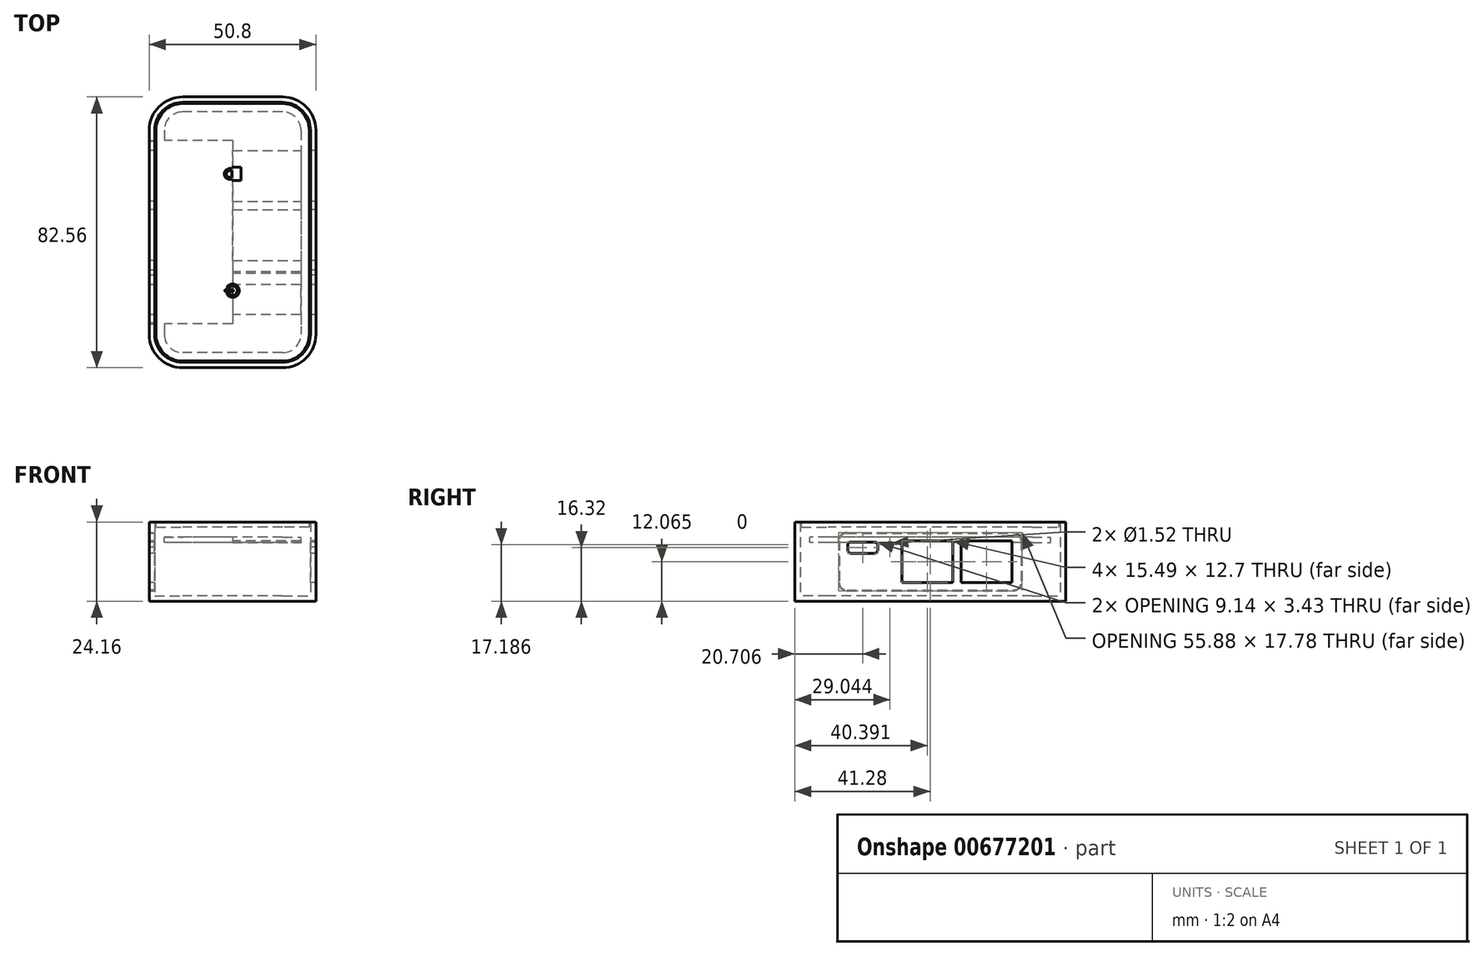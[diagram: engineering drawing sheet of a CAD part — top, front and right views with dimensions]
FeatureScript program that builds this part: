
annotation { "Feature Type Name" : "Feature", "Feature Type Description" : "" }
export const myFeature = defineFeature(function(context is Context, id is Id, definition is map)
    precondition{}
    {
        {
            var Q0;
            Q0=qCreatedBy(makeId("Top.planeOp"),FACE);
            var sketch = newSketch(context, id + "F0", { "sketchPlane" : qUnion([Q0])});
            skLineSegment(sketch, "E0.bottom", {"start": v(25.4, 41.28) * mm, "end": v(-25.4, 41.28) * mm});
            skLineSegment(sketch, "E0.top", {"start": v(25.4, -41.28) * mm, "end": v(-25.4, -41.28) * mm});
            skLineSegment(sketch, "E0.left", {"start": v(25.4, 41.28) * mm, "end": v(25.4, -41.28) * mm});
            skLineSegment(sketch, "E0.right", {"start": v(-25.4, 41.28) * mm, "end": v(-25.4, -41.28) * mm});
            skPoint(sketch, "E0.middle", {"position": v(0, 0) * mm});
            skSolve(sketch);
        }
        {
            var Q0;
            Q0=qSketchRegion(id+"F0",true);
            extrude(context, id + "F1", {"entities" : qUnion([Q0]), "depth" : 24.13 * mm, "offsetDistance" : 25.4 * mm});
        }
        {
            var Q0;
            Q0=makeQuery(id+"F1.opExtrude","SWEPT_EDGE",EDGE,{"disambiguationData":[OSD([sQuery(id+"F0.wireOp",EDGE,"E0.top"),sQuery(id+"F0.wireOp",EDGE,"E0.left")])]});
            var Q1;
            Q1=makeQuery(id+"F1.opExtrude","SWEPT_EDGE",EDGE,{"disambiguationData":[OSD([sQuery(id+"F0.wireOp",EDGE,"E0.top"),sQuery(id+"F0.wireOp",EDGE,"E0.right")])]});
            var Q2;
            Q2=makeQuery(id+"F1.opExtrude","SWEPT_EDGE",EDGE,{"disambiguationData":[OSD([sQuery(id+"F0.wireOp",EDGE,"E0.bottom"),sQuery(id+"F0.wireOp",EDGE,"E0.left")])]});
            var Q3;
            Q3=makeQuery(id+"F1.opExtrude","SWEPT_EDGE",EDGE,{"disambiguationData":[OSD([sQuery(id+"F0.wireOp",EDGE,"E0.bottom"),sQuery(id+"F0.wireOp",EDGE,"E0.right")])]});
            fillet(context, id + "F2", {"entities" : qUnion([Q0, Q1, Q2, Q3]), "radius" : 10.16 * mm, "tangentPropagation" : true, "allowEdgeOverflow" : false});
        }
        {
            var Q0;
            Q0=makeQuery(id+"F1.opExtrude","CAP_FACE",FACE,{"disambiguationData":[OSD([sQuery(id+"F0.wireOp",EDGE,"E0.bottom"),sQuery(id+"F0.wireOp",EDGE,"E0.top"),sQuery(id+"F0.wireOp",EDGE,"E0.left"),sQuery(id+"F0.wireOp",EDGE,"E0.right")])],"isStart":false});
            shell(context, id + "F3", {"entities" : qUnion([Q0]), "thickness" : 1.65 * mm});
        }
        {
            var Q0;
            Q0=makeQuery(id+"F1.opExtrude","CAP_FACE",FACE,{"disambiguationData":[OSD([sQuery(id+"F0.wireOp",EDGE,"E0.bottom"),sQuery(id+"F0.wireOp",EDGE,"E0.top"),sQuery(id+"F0.wireOp",EDGE,"E0.left"),sQuery(id+"F0.wireOp",EDGE,"E0.right")])],"isStart":false});
            var sketch = newSketch(context, id + "F4", { "sketchPlane" : qUnion([Q0])});
            skArc(sketch, "E1.0", {"start": v(-15.24, 39.24) * mm, "mid": v(-20.99, 36.86) * mm, "end": v(-23.37, 31.12) * mm});
            skLineSegment(sketch, "E1.1", {"start": v(15.24, 39.24) * mm, "end": v(-15.24, 39.24) * mm});
            skLineSegment(sketch, "E1.2", {"start": v(-23.37, 31.12) * mm, "end": v(-23.37, -31.12) * mm});
            skArc(sketch, "E1.3", {"start": v(23.37, 31.12) * mm, "mid": v(20.99, 36.86) * mm, "end": v(15.24, 39.24) * mm});
            skArc(sketch, "E1.4", {"start": v(-23.37, -31.12) * mm, "mid": v(-20.99, -36.86) * mm, "end": v(-15.24, -39.24) * mm});
            skLineSegment(sketch, "E1.5", {"start": v(15.24, -39.24) * mm, "end": v(-15.24, -39.24) * mm});
            skArc(sketch, "E1.6", {"start": v(15.24, -39.24) * mm, "mid": v(20.99, -36.86) * mm, "end": v(23.37, -31.12) * mm});
            skLineSegment(sketch, "E1.7", {"start": v(23.37, 31.12) * mm, "end": v(23.37, -31.12) * mm});
            skSolve(sketch);
        }
        {
            var Q0;
            Q0=qSketchRegion(id+"F4",true);
            extrude(context, id + "F5", {"entities" : qUnion([Q0]), "oppositeDirection" : true, "depth" : 6.35 * mm, "offsetDistance" : 25.4 * mm});
        }
        {
            var Q0;
            Q0=makeQuery(id+"F5.opExtrude","CAP_FACE",FACE,{"disambiguationData":[OSD([sQuery(id+"F4.wireOp",EDGE,"E1.0"),sQuery(id+"F4.wireOp",EDGE,"E1.1"),sQuery(id+"F4.wireOp",EDGE,"E1.2"),sQuery(id+"F4.wireOp",EDGE,"E1.3"),sQuery(id+"F4.wireOp",EDGE,"E1.4"),sQuery(id+"F4.wireOp",EDGE,"E1.5"),sQuery(id+"F4.wireOp",EDGE,"E1.6"),sQuery(id+"F4.wireOp",EDGE,"E1.7")])],"isStart":true});
            var sketch = newSketch(context, id + "F6", { "sketchPlane" : qUnion([Q0])});
            skLineSegment(sketch, "E2.0", {"start": v(15.24, 32.9) * mm, "end": v(-15.24, 32.9) * mm});
            skArc(sketch, "E2.1", {"start": v(17.02, 31.12) * mm, "mid": v(16.5, 32.37) * mm, "end": v(15.24, 32.9) * mm});
            skArc(sketch, "E2.2", {"start": v(-15.24, 32.9) * mm, "mid": v(-16.5, 32.37) * mm, "end": v(-17.02, 31.12) * mm});
            skLineSegment(sketch, "E2.3", {"start": v(17.02, 31.12) * mm, "end": v(17.02, -31.12) * mm});
            skLineSegment(sketch, "E2.4", {"start": v(-17.02, 31.12) * mm, "end": v(-17.02, -31.12) * mm});
            skArc(sketch, "E2.5", {"start": v(-17.02, -31.12) * mm, "mid": v(-16.5, -32.37) * mm, "end": v(-15.24, -32.9) * mm});
            skLineSegment(sketch, "E2.6", {"start": v(15.24, -32.9) * mm, "end": v(-15.24, -32.9) * mm});
            skArc(sketch, "E2.7", {"start": v(15.24, -32.9) * mm, "mid": v(16.5, -32.37) * mm, "end": v(17.02, -31.12) * mm});
            skSolve(sketch);
        }
        {
            var Q0;
            Q0=sQuery(id+"F6.wireOp",VERTEX,"E2.7.start");
            var Q1;
            Q1=qCreatedBy(makeId("Right.planeOp"),FACE);
            cPlane(context, id + "F7", {"entities" : qUnion([Q0, Q1]), "cplaneType" : CPlaneType.PLANE_POINT, "offset" : 25.4 * mm, "width" : 152.4 * mm, "height" : 152.4 * mm});
        }
        {
            var Q0;
            Q0=makeQuery(id+"F5.opExtrude","CAP_FACE",FACE,{"disambiguationData":[OSD([sQuery(id+"F4.wireOp",EDGE,"E1.0"),sQuery(id+"F4.wireOp",EDGE,"E1.1"),sQuery(id+"F4.wireOp",EDGE,"E1.2"),sQuery(id+"F4.wireOp",EDGE,"E1.3"),sQuery(id+"F4.wireOp",EDGE,"E1.4"),sQuery(id+"F4.wireOp",EDGE,"E1.5"),sQuery(id+"F4.wireOp",EDGE,"E1.6"),sQuery(id+"F4.wireOp",EDGE,"E1.7")])],"isStart":false});
            var Q1;
            Q1=makeQuery(id+"F5.opExtrude","SWEPT_FACE",FACE,{"disambiguationData":[OSD([sQuery(id+"F4.wireOp",EDGE,"E1.5")])]});
            var Q2;
            Q2=makeQuery(id+"F5.opExtrude","SWEPT_FACE",FACE,{"disambiguationData":[OSD([sQuery(id+"F4.wireOp",EDGE,"E1.6")])]});
            var Q3;
            Q3=makeQuery(id+"F5.opExtrude","SWEPT_FACE",FACE,{"disambiguationData":[OSD([sQuery(id+"F4.wireOp",EDGE,"E1.4")])]});
            var Q4;
            Q4=makeQuery(id+"F5.opExtrude","SWEPT_FACE",FACE,{"disambiguationData":[OSD([sQuery(id+"F4.wireOp",EDGE,"E1.7")])]});
            var Q5;
            Q5=makeQuery(id+"F5.opExtrude","SWEPT_FACE",FACE,{"disambiguationData":[OSD([sQuery(id+"F4.wireOp",EDGE,"E1.3")])]});
            var Q6;
            Q6=makeQuery(id+"F5.opExtrude","SWEPT_FACE",FACE,{"disambiguationData":[OSD([sQuery(id+"F4.wireOp",EDGE,"E1.1")])]});
            var Q7;
            Q7=makeQuery(id+"F5.opExtrude","SWEPT_FACE",FACE,{"disambiguationData":[OSD([sQuery(id+"F4.wireOp",EDGE,"E1.0")])]});
            var Q8;
            Q8=makeQuery(id+"F5.opExtrude","SWEPT_FACE",FACE,{"disambiguationData":[OSD([sQuery(id+"F4.wireOp",EDGE,"E1.2")])]});
            shell(context, id + "F8", {"entities" : qUnion([Q0, Q1, Q2, Q3, Q4, Q5, Q6, Q7, Q8]), "thickness" : 1.52 * mm});
        }
        {
            var Q0;
            Q0=makeQuery(id+"F4.imprint","IMPRINT",FACE,{"disambiguationData":[TD([[makeQuery(id+"F4.imprint","IMPRINT",EDGE,{"derivedFrom":sQuery(id+"F4.wireOp",EDGE,"E1.0")}),1.0]])]});
            var sketch = newSketch(context, id + "F9", { "sketchPlane" : qUnion([Q0])});
            skLineSegment(sketch, "E3.bottom", {"start": v(2.54, 22.86) * mm, "end": v(-2.54, 22.86) * mm});
            skLineSegment(sketch, "E3.top", {"start": v(2.54, 12.7) * mm, "end": v(-2.54, 12.7) * mm});
            skLineSegment(sketch, "E3.left", {"start": v(5.08, 20.32) * mm, "end": v(5.08, 15.24) * mm});
            skLineSegment(sketch, "E3.right", {"start": v(-5.08, 20.32) * mm, "end": v(-5.08, 15.24) * mm});
            skPoint(sketch, "E3.middle", {"position": v(0, 17.78) * mm});
            skPoint(sketch, "E4.visualSharp", {"position": v(-5.08, 22.86) * mm});
            skArc(sketch, "E4.filletArc", {"start": v(-2.54, 22.86) * mm, "mid": v(-4.34, 22.12) * mm, "end": v(-5.08, 20.32) * mm});
            skPoint(sketch, "E5.visualSharp", {"position": v(5.08, 22.86) * mm});
            skArc(sketch, "E5.filletArc", {"start": v(5.08, 20.32) * mm, "mid": v(4.34, 22.12) * mm, "end": v(2.54, 22.86) * mm});
            skPoint(sketch, "E6.visualSharp", {"position": v(5.08, 12.7) * mm});
            skArc(sketch, "E6.filletArc", {"start": v(2.54, 12.7) * mm, "mid": v(4.34, 13.44) * mm, "end": v(5.08, 15.24) * mm});
            skPoint(sketch, "E7.visualSharp", {"position": v(-5.08, 12.7) * mm});
            skArc(sketch, "E7.filletArc", {"start": v(-5.08, 15.24) * mm, "mid": v(-4.34, 13.44) * mm, "end": v(-2.54, 12.7) * mm});
            skArc(sketch, "E8.MirrorCS", {"start": v(-2.54, -22.86) * mm, "mid": v(-4.34, -22.12) * mm, "end": v(-5.08, -20.32) * mm});
            skLineSegment(sketch, "E9.MirrorCS", {"start": v(-5.08, -20.32) * mm, "end": v(-5.08, -15.24) * mm});
            skLineSegment(sketch, "E10.MirrorCS", {"start": v(5.08, -20.32) * mm, "end": v(5.08, -15.24) * mm});
            skArc(sketch, "E11.MirrorCS", {"start": v(2.54, -12.7) * mm, "mid": v(4.34, -13.44) * mm, "end": v(5.08, -15.24) * mm});
            skArc(sketch, "E12.MirrorCS", {"start": v(-5.08, -15.24) * mm, "mid": v(-4.34, -13.44) * mm, "end": v(-2.54, -12.7) * mm});
            skLineSegment(sketch, "E13.MirrorCS", {"start": v(2.54, -12.7) * mm, "end": v(-2.54, -12.7) * mm});
            skArc(sketch, "E14.MirrorCS", {"start": v(5.08, -20.32) * mm, "mid": v(4.34, -22.12) * mm, "end": v(2.54, -22.86) * mm});
            skLineSegment(sketch, "E15.MirrorCS", {"start": v(2.54, -22.86) * mm, "end": v(-2.54, -22.86) * mm});
            skSolve(sketch);
        }
        {
            var Q0;
            Q0=makeQuery(id+"F5.opExtrude","CAP_FACE",FACE,{"disambiguationData":[OSD([sQuery(id+"F4.wireOp",EDGE,"E1.0"),sQuery(id+"F4.wireOp",EDGE,"E1.1"),sQuery(id+"F4.wireOp",EDGE,"E1.2"),sQuery(id+"F4.wireOp",EDGE,"E1.3"),sQuery(id+"F4.wireOp",EDGE,"E1.4"),sQuery(id+"F4.wireOp",EDGE,"E1.5"),sQuery(id+"F4.wireOp",EDGE,"E1.6"),sQuery(id+"F4.wireOp",EDGE,"E1.7")])],"isStart":true});
            cPlane(context, id + "F10", {"entities" : qUnion([Q0]), "cplaneType" : CPlaneType.OFFSET, "offset" : 0 * mm, "width" : 152.4 * mm, "height" : 152.4 * mm});
        }
        {
            var Q0;
            Q0=qCreatedBy(id+"F10.planeOp",FACE);
            var sketch = newSketch(context, id + "F11", { "sketchPlane" : qUnion([Q0])});
            skArc(sketch, "E16.0", {"start": v(2.54, -12.95) * mm, "mid": v(4.16, -13.62) * mm, "end": v(4.83, -15.24) * mm});
            skLineSegment(sketch, "E16.1", {"start": v(4.83, -20.32) * mm, "end": v(4.83, -15.24) * mm});
            skLineSegment(sketch, "E16.2", {"start": v(2.54, -12.95) * mm, "end": v(-2.54, -12.95) * mm});
            skArc(sketch, "E16.3", {"start": v(4.83, -20.32) * mm, "mid": v(4.16, -21.94) * mm, "end": v(2.54, -22.6) * mm});
            skArc(sketch, "E16.4", {"start": v(-4.83, -15.24) * mm, "mid": v(-4.16, -13.62) * mm, "end": v(-2.54, -12.95) * mm});
            skLineSegment(sketch, "E16.5", {"start": v(-4.83, -20.32) * mm, "end": v(-4.83, -15.24) * mm});
            skArc(sketch, "E16.6", {"start": v(-2.54, -22.6) * mm, "mid": v(-4.16, -21.94) * mm, "end": v(-4.83, -20.32) * mm});
            skLineSegment(sketch, "E16.7", {"start": v(2.54, -22.6) * mm, "end": v(-2.54, -22.6) * mm});
            skArc(sketch, "E17.0", {"start": v(4.83, 20.32) * mm, "mid": v(4.16, 21.94) * mm, "end": v(2.54, 22.6) * mm});
            skLineSegment(sketch, "E17.1", {"start": v(4.83, 20.32) * mm, "end": v(4.83, 15.24) * mm});
            skLineSegment(sketch, "E17.2", {"start": v(2.54, 22.6) * mm, "end": v(-2.54, 22.6) * mm});
            skArc(sketch, "E17.3", {"start": v(2.54, 12.95) * mm, "mid": v(4.16, 13.62) * mm, "end": v(4.83, 15.24) * mm});
            skArc(sketch, "E17.4", {"start": v(-2.54, 22.6) * mm, "mid": v(-4.16, 21.94) * mm, "end": v(-4.83, 20.32) * mm});
            skLineSegment(sketch, "E17.5", {"start": v(-4.83, 20.32) * mm, "end": v(-4.83, 15.24) * mm});
            skArc(sketch, "E17.6", {"start": v(-4.83, 15.24) * mm, "mid": v(-4.16, 13.62) * mm, "end": v(-2.54, 12.95) * mm});
            skLineSegment(sketch, "E17.7", {"start": v(2.54, 12.95) * mm, "end": v(-2.54, 12.95) * mm});
            skSolve(sketch);
        }
        {
            var Q0;
            Q0=makeQuery(id+"F8.opShell","OFFSET_FACE",FACE,{"disambiguationData":[OSD([sQuery(id+"F4.wireOp",EDGE,"E1.0"),sQuery(id+"F4.wireOp",EDGE,"E1.1"),sQuery(id+"F4.wireOp",EDGE,"E1.2"),sQuery(id+"F4.wireOp",EDGE,"E1.3"),sQuery(id+"F4.wireOp",EDGE,"E1.4"),sQuery(id+"F4.wireOp",EDGE,"E1.5"),sQuery(id+"F4.wireOp",EDGE,"E1.6"),sQuery(id+"F4.wireOp",EDGE,"E1.7")])]});
            cPlane(context, id + "F12", {"entities" : qUnion([Q0]), "cplaneType" : CPlaneType.OFFSET, "offset" : 3.05 * mm, "width" : 152.4 * mm, "height" : 152.4 * mm});
        }
        {
            var Q0;
            Q0=qCreatedBy(id+"F12.planeOp",FACE);
            var sketch = newSketch(context, id + "F13", { "sketchPlane" : qUnion([Q0])});
            skLineSegment(sketch, "E18.0", {"start": v(-20.83, -31.12) * mm, "end": v(-20.83, 31.12) * mm});
            skArc(sketch, "E18.1", {"start": v(-15.24, -36.7) * mm, "mid": v(-19.2, -35.07) * mm, "end": v(-20.83, -31.12) * mm});
            skArc(sketch, "E18.2", {"start": v(-20.83, 31.12) * mm, "mid": v(-19.2, 35.07) * mm, "end": v(-15.24, 36.7) * mm});
            skLineSegment(sketch, "E18.3", {"start": v(15.24, -36.7) * mm, "end": v(-15.24, -36.7) * mm});
            skLineSegment(sketch, "E18.4", {"start": v(15.24, 36.7) * mm, "end": v(-15.24, 36.7) * mm});
            skArc(sketch, "E18.5", {"start": v(15.24, 36.7) * mm, "mid": v(19.2, 35.07) * mm, "end": v(20.83, 31.12) * mm});
            skLineSegment(sketch, "E18.6", {"start": v(20.83, -31.12) * mm, "end": v(20.83, 31.12) * mm});
            skArc(sketch, "E18.7", {"start": v(20.83, -31.12) * mm, "mid": v(19.2, -35.07) * mm, "end": v(15.24, -36.7) * mm});
            skSolve(sketch);
        }
        {
            var Q0;
            Q0=qSketchRegion(id+"F13",true);
            extrude(context, id + "F14", {"entities" : qUnion([Q0]), "depth" : 1.65 * mm, "offsetDistance" : 25.4 * mm});
        }
        {
            var Q0;
            Q0=makeQuery(id+"F5.opExtrude","CAP_FACE",FACE,{"disambiguationData":[OSD([sQuery(id+"F4.wireOp",EDGE,"E1.0"),sQuery(id+"F4.wireOp",EDGE,"E1.1"),sQuery(id+"F4.wireOp",EDGE,"E1.2"),sQuery(id+"F4.wireOp",EDGE,"E1.3"),sQuery(id+"F4.wireOp",EDGE,"E1.4"),sQuery(id+"F4.wireOp",EDGE,"E1.5"),sQuery(id+"F4.wireOp",EDGE,"E1.6"),sQuery(id+"F4.wireOp",EDGE,"E1.7")])],"isStart":true});
            var sketch = newSketch(context, id + "F15", { "sketchPlane" : qUnion([Q0])});
            skPoint(sketch, "E19", {"position": v(-4.28, -17.3) * mm});
            skPoint(sketch, "E20", {"position": v(-4.83, -17.78) * mm});
            skPoint(sketch, "E21", {"position": v(0, -22.6) * mm});
            skLineSegment(sketch, "E22", {"start": v(-4.83, -17.78) * mm, "end": v(3.41, -17.78) * mm, "construction": true});
            skLineSegment(sketch, "E23", {"start": v(0, -22.6) * mm, "end": v(0, -17.78) * mm, "construction": true});
            skArc(sketch, "E24", {"start": v(-2, -18.1) * mm, "mid": v(-2, -18.1) * mm, "end": v(-2, -18.1) * mm});
            skArc(sketch, "E25", {"start": v(-0.99, -18.77) * mm, "mid": v(1.4, -17.78) * mm, "end": v(-0.99, -16.8) * mm});
            skArc(sketch, "E26", {"start": v(0, -18.1) * mm, "mid": v(0.32, -17.78) * mm, "end": v(0, -17.46) * mm});
            skArc(sketch, "E27", {"start": v(-2, -17.46) * mm, "mid": v(-2.35, -17.78) * mm, "end": v(-2, -18.1) * mm});
            skLineSegment(sketch, "E28", {"start": v(-2.03, -18.1) * mm, "end": v(0, -18.1) * mm});
            skLineSegment(sketch, "E29", {"start": v(0, -17.46) * mm, "end": v(-2.03, -17.46) * mm});
            skLineSegment(sketch, "E30", {"start": v(-1.57, -18.73) * mm, "end": v(-1.08, -18.73) * mm});
            skLineSegment(sketch, "E31", {"start": v(-1.57, -16.83) * mm, "end": v(-1.08, -16.83) * mm});
            skArc(sketch, "E32.trimOffspring", {"start": v(-1.67, -18.93) * mm, "mid": v(2.03, -17.78) * mm, "end": v(-1.67, -16.63) * mm});
            skArc(sketch, "E33.trimOffspring", {"start": v(-2, -17.46) * mm, "mid": v(-2, -17.46) * mm, "end": v(-2, -17.46) * mm});
            skPoint(sketch, "E34.visualSharp", {"position": v(-1.8, -18.73) * mm});
            skArc(sketch, "E34.filletArc", {"start": v(-1.57, -18.73) * mm, "mid": v(-1.68, -18.8) * mm, "end": v(-1.67, -18.93) * mm});
            skPoint(sketch, "E35.visualSharp", {"position": v(-1.02, -18.73) * mm});
            skArc(sketch, "E35.filletArc", {"start": v(-0.99, -18.77) * mm, "mid": v(-1.03, -18.74) * mm, "end": v(-1.08, -18.73) * mm});
            skPoint(sketch, "E36.visualSharp", {"position": v(-1.02, -16.83) * mm});
            skArc(sketch, "E36.filletArc", {"start": v(-1.08, -16.83) * mm, "mid": v(-1.03, -16.82) * mm, "end": v(-0.99, -16.8) * mm});
            skPoint(sketch, "E37.visualSharp", {"position": v(-1.8, -16.83) * mm});
            skArc(sketch, "E37.filletArc", {"start": v(-1.67, -16.63) * mm, "mid": v(-1.68, -16.76) * mm, "end": v(-1.57, -16.83) * mm});
            skLineSegment(sketch, "E38.0", {"start": v(2.54, -22.6) * mm, "end": v(-2.54, -22.6) * mm, "construction": true});
            skLineSegment(sketch, "E39.0", {"start": v(-4.83, -20.32) * mm, "end": v(-4.83, -15.24) * mm, "construction": true});
            skSolve(sketch);
        }
        {
            var Q0;
            Q0=qSketchRegion(id+"F15",true);
            extrude(context, id + "F16", {"entities" : qUnion([Q0]), "depth" : 0.03 * mm, "offsetDistance" : 25.4 * mm});
        }
        {
            var Q0;
            Q0=makeQuery(id+"F5.opExtrude","CAP_FACE",FACE,{"disambiguationData":[OSD([sQuery(id+"F4.wireOp",EDGE,"E1.0"),sQuery(id+"F4.wireOp",EDGE,"E1.1"),sQuery(id+"F4.wireOp",EDGE,"E1.2"),sQuery(id+"F4.wireOp",EDGE,"E1.3"),sQuery(id+"F4.wireOp",EDGE,"E1.4"),sQuery(id+"F4.wireOp",EDGE,"E1.5"),sQuery(id+"F4.wireOp",EDGE,"E1.6"),sQuery(id+"F4.wireOp",EDGE,"E1.7")])],"isStart":true});
            var sketch = newSketch(context, id + "F17", { "sketchPlane" : qUnion([Q0])});
            skLineSegment(sketch, "E40.0", {"start": v(-4.83, 20.32) * mm, "end": v(-4.83, 15.24) * mm, "construction": true});
            skLineSegment(sketch, "E41.0", {"start": v(-2.54, 12.95) * mm, "end": v(2.54, 12.95) * mm, "construction": true});
            skPoint(sketch, "E42", {"position": v(-4.83, 17.78) * mm});
            skPoint(sketch, "E43", {"position": v(0, 12.95) * mm});
            skLineSegment(sketch, "E44", {"start": v(0, 12.95) * mm, "end": v(0, 19.74) * mm, "construction": true});
            skLineSegment(sketch, "E45", {"start": v(-4.83, 17.78) * mm, "end": v(0, 17.78) * mm, "construction": true});
            skLineSegment(sketch, "E46.bottom", {"start": v(2.54, 19.81) * mm, "end": v(-0.25, 19.81) * mm});
            skLineSegment(sketch, "E46.top", {"start": v(2.54, 15.75) * mm, "end": v(-0.25, 15.75) * mm});
            skLineSegment(sketch, "E46.left", {"start": v(2.54, 19.81) * mm, "end": v(2.54, 15.75) * mm});
            skLineSegment(sketch, "E46.right", {"start": v(-0.25, 19.81) * mm, "end": v(-0.25, 19.43) * mm});
            skPoint(sketch, "E46.middle", {"position": v(1.14, 17.78) * mm});
            skArc(sketch, "E47", {"start": v(-0.89, 19.43) * mm, "mid": v(-2.54, 17.78) * mm, "end": v(-0.89, 16.13) * mm});
            skArc(sketch, "E48", {"start": v(-0.89, 18.8) * mm, "mid": v(-1.9, 17.78) * mm, "end": v(-0.89, 16.76) * mm});
            skLineSegment(sketch, "E49", {"start": v(-0.89, 16.13) * mm, "end": v(-0.25, 16.13) * mm});
            skLineSegment(sketch, "E50", {"start": v(-0.89, 16.76) * mm, "end": v(-0.25, 16.76) * mm});
            skLineSegment(sketch, "E51", {"start": v(-0.89, 18.8) * mm, "end": v(-0.25, 18.8) * mm});
            skLineSegment(sketch, "E52", {"start": v(-0.89, 19.43) * mm, "end": v(-0.25, 19.43) * mm});
            skLineSegment(sketch, "E53.trimOffspring", {"start": v(-0.25, 16.13) * mm, "end": v(-0.25, 15.75) * mm});
            skLineSegment(sketch, "E54.trimOffspring", {"start": v(-0.25, 18.8) * mm, "end": v(-0.25, 16.76) * mm});
            skSolve(sketch);
        }
        {
            var Q0;
            Q0=qSketchRegion(id+"F17",true);
            extrude(context, id + "F18", {"entities" : qUnion([Q0]), "depth" : 0.03 * mm, "offsetDistance" : 25.4 * mm});
        }
        {
            var Q0;
            Q0=qCreatedBy(makeId("Right.planeOp"),FACE);
            var sketch = newSketch(context, id + "F19", { "sketchPlane" : qUnion([Q0])});
            skLineSegment(sketch, "E55", {"start": v(0, 33.17) * mm, "end": v(0, -9.04) * mm, "construction": true});
            skLineSegment(sketch, "E56.bottom", {"start": v(-27.94, 20.96) * mm, "end": v(27.94, 20.96) * mm});
            skLineSegment(sketch, "E56.top", {"start": v(-27.94, 3.18) * mm, "end": v(27.94, 3.18) * mm});
            skLineSegment(sketch, "E56.left", {"start": v(-27.94, 20.96) * mm, "end": v(-27.94, 3.18) * mm});
            skLineSegment(sketch, "E56.right", {"start": v(27.94, 20.96) * mm, "end": v(27.94, 3.18) * mm});
            skPoint(sketch, "E56.middle", {"position": v(0, 12.06) * mm});
            skPoint(sketch, "E57", {"position": v(-27.94, 12.07) * mm});
            skPoint(sketch, "E58", {"position": v(-31.12, 12.07) * mm});
            skSolve(sketch);
        }
        {
            var Q0;
            Q0 = qSketchRegion(id + "F19", true);
            extrude(context, id + "F20", {"entities" : qUnion([Q0]), "operationType" : NewBodyOperationType.REMOVE, "endBound" : BoundingType.THROUGH_ALL, "oppositeDirection" : true, "depth" : 25.4 * mm, "offsetDistance" : 25.4 * mm});
        }
        {
            var Q0;
            Q0=makeQuery(id+"F20.boolean.opBoolean","COPY",EDGE,{"derivedFrom":makeQuery(id+"F20.opExtrude","SWEPT_EDGE",EDGE,{"disambiguationData":[OSD([sQuery(id+"F19.wireOp",EDGE,"E56.bottom"),sQuery(id+"F19.wireOp",EDGE,"E56.right")])]})});
            var Q1;
            Q1=makeQuery(id+"F20.boolean.opBoolean","COPY",EDGE,{"derivedFrom":makeQuery(id+"F20.opExtrude","SWEPT_EDGE",EDGE,{"disambiguationData":[OSD([sQuery(id+"F19.wireOp",EDGE,"E56.bottom"),sQuery(id+"F19.wireOp",EDGE,"E56.left")])]})});
            var Q2;
            Q2=makeQuery(id+"F20.boolean.opBoolean","COPY",EDGE,{"derivedFrom":makeQuery(id+"F20.opExtrude","SWEPT_EDGE",EDGE,{"disambiguationData":[OSD([sQuery(id+"F19.wireOp",EDGE,"E56.top"),sQuery(id+"F19.wireOp",EDGE,"E56.left")])]})});
            var Q3;
            Q3=makeQuery(id+"F20.boolean.opBoolean","COPY",EDGE,{"derivedFrom":makeQuery(id+"F20.opExtrude","SWEPT_EDGE",EDGE,{"disambiguationData":[OSD([sQuery(id+"F19.wireOp",EDGE,"E56.top"),sQuery(id+"F19.wireOp",EDGE,"E56.right")])]})});
            fillet(context, id + "F21", {"entities" : qUnion([Q0, Q1, Q2, Q3]), "radius" : 2.54 * mm, "tangentPropagation" : true, "allowEdgeOverflow" : false});
        }
        {
            var Q0;
            Q0=makeQuery(id+"F1.opExtrude","SWEPT_FACE",FACE,{"disambiguationData":[OSD([sQuery(id+"F0.wireOp",EDGE,"E0.right")])]});
            var sketch = newSketch(context, id + "F22", { "sketchPlane" : qUnion([Q0])});
            skArc(sketch, "E59.0", {"start": v(27.69, 5.72) * mm, "mid": v(27.02, 4.1) * mm, "end": v(25.4, 3.43) * mm});
            skLineSegment(sketch, "E59.1", {"start": v(27.69, 18.41) * mm, "end": v(27.69, 5.72) * mm});
            skLineSegment(sketch, "E59.2", {"start": v(25.4, 3.43) * mm, "end": v(-25.4, 3.43) * mm});
            skArc(sketch, "E59.3", {"start": v(25.4, 20.7) * mm, "mid": v(27.02, 20.03) * mm, "end": v(27.69, 18.41) * mm});
            skArc(sketch, "E59.4", {"start": v(-25.4, 3.43) * mm, "mid": v(-27.02, 4.1) * mm, "end": v(-27.69, 5.72) * mm});
            skLineSegment(sketch, "E59.5", {"start": v(-27.69, 18.41) * mm, "end": v(-27.69, 5.72) * mm});
            skArc(sketch, "E59.6", {"start": v(-27.69, 18.41) * mm, "mid": v(-27.02, 20.03) * mm, "end": v(-25.4, 20.7) * mm});
            skLineSegment(sketch, "E59.7", {"start": v(25.4, 20.7) * mm, "end": v(-25.4, 20.7) * mm});
            skSolve(sketch);
        }
        {
            var Q0;
            Q0 = qSketchRegion(id + "F22", true);
            extrude(context, id + "F23", {"entities" : qUnion([Q0]), "oppositeDirection" : true, "depth" : 1.52 * mm, "offsetDistance" : 25.4 * mm});
        }
        {
            var Q0;
            Q0=makeQuery(id+"F1.opExtrude","SWEPT_FACE",FACE,{"disambiguationData":[OSD([sQuery(id+"F0.wireOp",EDGE,"E0.right")])]});
            var sketch = newSketch(context, id + "F24", { "sketchPlane" : qUnion([Q0])});
            skLineSegment(sketch, "E60.bottom", {"start": v(-24.9, 18.42) * mm, "end": v(-9.4, 18.42) * mm});
            skLineSegment(sketch, "E60.top", {"start": v(-24.9, 5.72) * mm, "end": v(-9.4, 5.72) * mm});
            skLineSegment(sketch, "E60.left", {"start": v(-24.9, 18.41) * mm, "end": v(-24.9, 5.72) * mm});
            skLineSegment(sketch, "E60.right", {"start": v(-9.4, 18.42) * mm, "end": v(-9.4, 5.72) * mm});
            skPoint(sketch, "E60.middle", {"position": v(-17.14, 12.07) * mm});
            skLineSegment(sketch, "E61.bottom", {"start": v(-6.86, 18.41) * mm, "end": v(8.64, 18.41) * mm});
            skLineSegment(sketch, "E61.top", {"start": v(-6.86, 5.72) * mm, "end": v(8.64, 5.72) * mm});
            skLineSegment(sketch, "E61.left", {"start": v(-6.86, 18.41) * mm, "end": v(-6.86, 5.72) * mm});
            skLineSegment(sketch, "E61.right", {"start": v(8.64, 18.41) * mm, "end": v(8.64, 5.72) * mm});
            skPoint(sketch, "E61.middle", {"position": v(0.89, 12.07) * mm});
            skPoint(sketch, "E61.middle.positionSnap0", {"position": v(-9.4, 12.07) * mm});
            skPoint(sketch, "E61.centerSnap0", {"position": v(-9.4, 12.07) * mm});
            skLineSegment(sketch, "E62.bottom", {"start": v(25.15, 14.6) * mm, "end": v(16, 14.6) * mm});
            skLineSegment(sketch, "E62.top", {"start": v(25.15, 18.03) * mm, "end": v(16, 18.03) * mm});
            skLineSegment(sketch, "E62.left", {"start": v(25.15, 14.6) * mm, "end": v(25.15, 18.03) * mm});
            skLineSegment(sketch, "E62.right", {"start": v(16, 14.6) * mm, "end": v(16, 18.03) * mm});
            skPoint(sketch, "E62.middle", {"position": v(20.57, 16.32) * mm});
            skCircle(sketch, "E63", {"center": v(12.24, 17.19) * mm, "radius": 0.76 * mm});
            skPoint(sketch, "E64", {"position": v(-27.94, 12.07) * mm});
            skSolve(sketch);
        }
        {
            var Q0;
            Q0 = qSketchRegion(id + "F24", true);
            extrude(context, id + "F25", {"entities" : qUnion([Q0]), "operationType" : NewBodyOperationType.REMOVE, "endBound" : BoundingType.THROUGH_ALL, "oppositeDirection" : true, "depth" : 25.4 * mm, "offsetDistance" : 25.4 * mm});
        }
        {
            var Q0;
            Q0=makeQuery(id+"F25.boolean.opBoolean","COPY",EDGE,{"derivedFrom":makeQuery(id+"F25.opExtrude","SWEPT_EDGE",EDGE,{"disambiguationData":[OSD([sQuery(id+"F24.wireOp",EDGE,"E62.top"),sQuery(id+"F24.wireOp",EDGE,"E62.right")])]})});
            var Q1;
            Q1=makeQuery(id+"F25.boolean.opBoolean","COPY",EDGE,{"derivedFrom":makeQuery(id+"F25.opExtrude","SWEPT_EDGE",EDGE,{"disambiguationData":[OSD([sQuery(id+"F24.wireOp",EDGE,"E62.top"),sQuery(id+"F24.wireOp",EDGE,"E62.left")])]})});
            var Q2;
            Q2=makeQuery(id+"F25.boolean.opBoolean","COPY",EDGE,{"derivedFrom":makeQuery(id+"F25.opExtrude","SWEPT_EDGE",EDGE,{"disambiguationData":[OSD([sQuery(id+"F24.wireOp",EDGE,"E62.bottom"),sQuery(id+"F24.wireOp",EDGE,"E62.right")])]})});
            var Q3;
            Q3=makeQuery(id+"F25.boolean.opBoolean","COPY",EDGE,{"derivedFrom":makeQuery(id+"F25.opExtrude","SWEPT_EDGE",EDGE,{"disambiguationData":[OSD([sQuery(id+"F24.wireOp",EDGE,"E62.bottom"),sQuery(id+"F24.wireOp",EDGE,"E62.left")])]})});
            fillet(context, id + "F26", {"entities" : qUnion([Q0, Q1, Q2, Q3]), "radius" : 1.02 * mm, "tangentPropagation" : true, "allowEdgeOverflow" : false});
        }
    });
